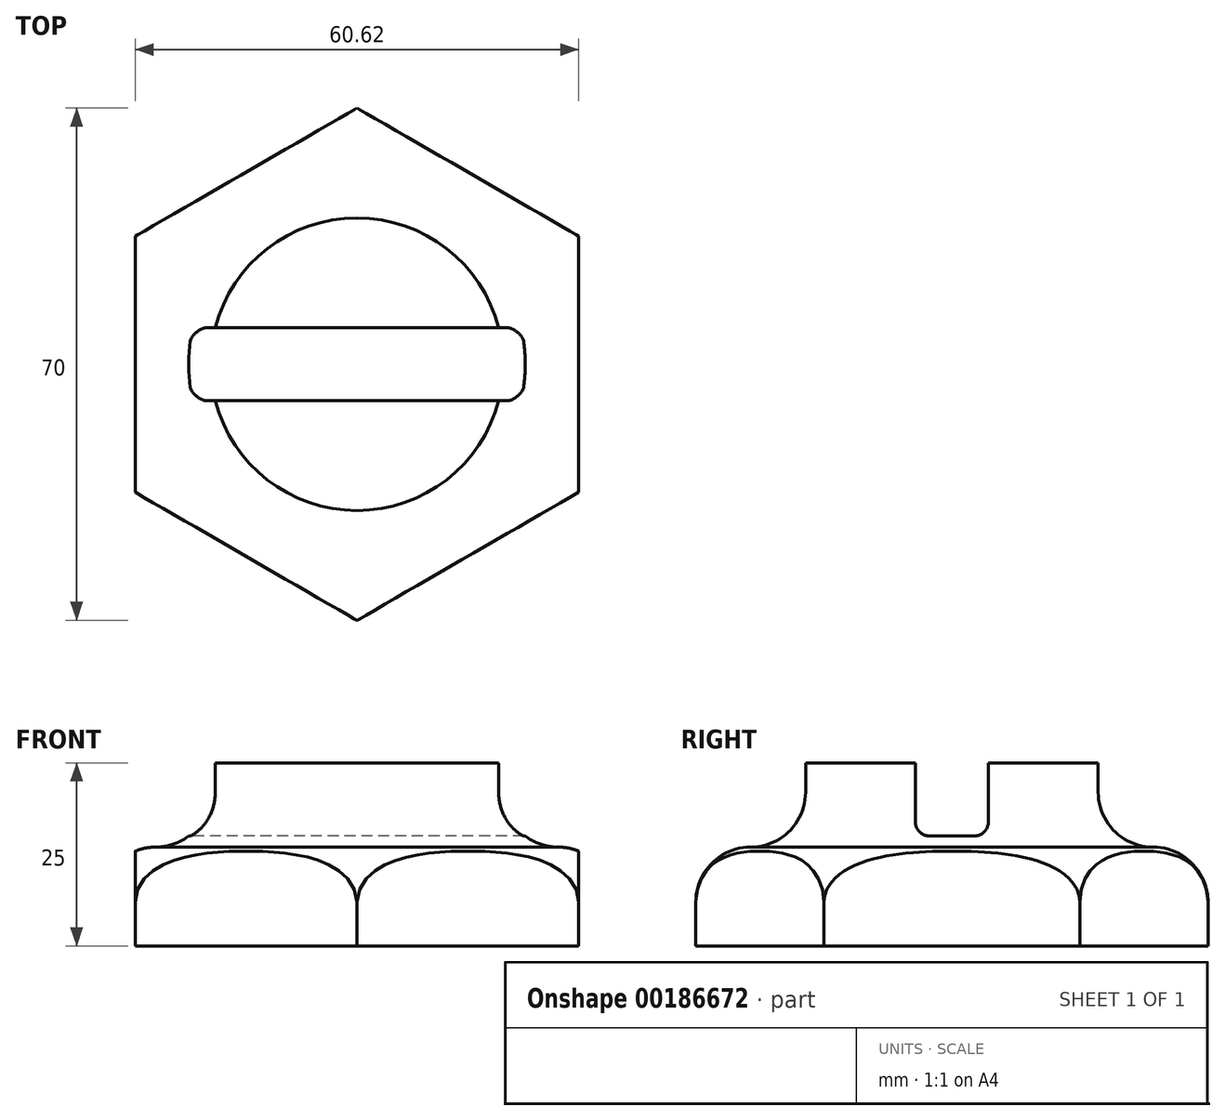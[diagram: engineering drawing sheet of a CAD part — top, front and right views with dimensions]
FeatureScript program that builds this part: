
annotation { "Feature Type Name" : "Feature", "Feature Type Description" : "" }
export const myFeature = defineFeature(function(context is Context, id is Id, definition is map)
    precondition{}
    {
        {
            var Q0;
            Q0=qCreatedBy(makeId("Top.planeOp"),FACE);
            var sketch = newSketch(context, id + "F0", { "sketchPlane" : qUnion([Q0])});
            skCircle(sketch, "E0.cCircle", {"center": v(0, 0) * mm, "radius": 35 * mm, "construction": true});
            skLineSegment(sketch, "E0.0", {"start": v(0, -35) * mm, "end": v(-30.31, -17.5) * mm});
            skLineSegment(sketch, "E0.1", {"start": v(-30.31, -17.5) * mm, "end": v(-30.31, 17.5) * mm});
            skLineSegment(sketch, "E0.2", {"start": v(-30.31, 17.5) * mm, "end": v(0, 35) * mm});
            skLineSegment(sketch, "E0.3", {"start": v(0, 35) * mm, "end": v(30.31, 17.5) * mm});
            skLineSegment(sketch, "E0.4", {"start": v(30.31, 17.5) * mm, "end": v(30.31, -17.5) * mm});
            skLineSegment(sketch, "E0.5", {"start": v(30.31, -17.5) * mm, "end": v(0, -35) * mm});
            skSolve(sketch);
        }
        {
            var Q0;
            Q0=qSketchRegion(id+"F0",true);
            extrude(context, id + "F1", {"entities" : qUnion([Q0]), "depth" : 25 * mm});
        }
        {
            var Q0;
            Q0=qCreatedBy(makeId("Right.planeOp"),FACE);
            var sketch = newSketch(context, id + "F2", { "sketchPlane" : qUnion([Q0])});
            skPoint(sketch, "E1.0", {"position": v(-35, 0) * mm});
            skLineSegment(sketch, "E2", {"start": v(-20, 21) * mm, "end": v(-20, 25) * mm});
            skArc(sketch, "E3", {"start": v(-27.5, 13.5) * mm, "mid": v(-32.8, 11.3) * mm, "end": v(-35, 6) * mm});
            skArc(sketch, "E4", {"start": v(-27.5, 13.5) * mm, "mid": v(-22.2, 15.7) * mm, "end": v(-20, 21) * mm});
            skLineSegment(sketch, "E5", {"start": v(-20, 25) * mm, "end": v(-17.5, 25) * mm});
            skLineSegment(sketch, "E6", {"start": v(-35, 6) * mm, "end": v(-35, 0) * mm});
            skLineSegment(sketch, "E7", {"start": v(-20, 25) * mm, "end": v(0, 25) * mm});
            skLineSegment(sketch, "E8", {"start": v(-35, 0) * mm, "end": v(0, 0) * mm});
            skLineSegment(sketch, "E9", {"start": v(0, 0) * mm, "end": v(0, 25) * mm});
            skSolve(sketch);
        }
        {
            var Q0;
            Q0=qCreatedBy(makeId("Right.planeOp"),FACE);
            var sketch = newSketch(context, id + "F3", { "sketchPlane" : qUnion([Q0])});
            skLineSegment(sketch, "E10", {"start": v(0, 0) * mm, "end": v(0, 25) * mm});
            skSolve(sketch);
        }
        {
            var Q0;
            Q0=qSketchRegion(id+"F2",true);
            var Q1;
            Q1=sQuery(id+"F3.wireOp",EDGE,"E10");
            revolve(context, id + "F4", {"operationType" : NewBodyOperationType.INTERSECT, "entities" : qUnion([Q0]), "axis" : qUnion([Q1]), "revolveType" : RevolveType.ONE_DIRECTION, "oppositeDirection" : true, "angle" : 360 * degree});
        }
        {
            var Q0;
            Q0=qCreatedBy(makeId("Right.planeOp"),FACE);
            var sketch = newSketch(context, id + "F5", { "sketchPlane" : qUnion([Q0])});
            skLineSegment(sketch, "E11", {"start": v(0, 0) * mm, "end": v(0, 25) * mm});
            skLineSegment(sketch, "E12", {"start": v(0, 25) * mm, "end": v(5, 25) * mm});
            skLineSegment(sketch, "E13", {"start": v(5, 25) * mm, "end": v(-5, 25) * mm});
            skLineSegment(sketch, "E14", {"start": v(-5, 25) * mm, "end": v(-5, 15) * mm});
            skLineSegment(sketch, "E15", {"start": v(-5, 15) * mm, "end": v(5, 15) * mm});
            skLineSegment(sketch, "E16", {"start": v(5, 15) * mm, "end": v(5, 25) * mm});
            skLineSegment(sketch, "E17.bottom", {"start": v(-5, 25) * mm, "end": v(5, 25) * mm});
            skLineSegment(sketch, "E17.right", {"start": v(5, 25) * mm, "end": v(5, 15) * mm});
            skSolve(sketch);
        }
        {
            var Q0;
            Q0=qSketchRegion(id+"F5",true);
            var Q1;
            Q1=makeQuery(id+"F1.opExtrude","SWEPT_FACE",FACE,{"disambiguationData":[OSD([sQuery(id+"F0.wireOp",EDGE,"E0.4")])]});
            extrude(context, id + "F6", {"entities" : qUnion([Q0, Q1]), "operationType" : NewBodyOperationType.REMOVE, "depth" : 49.5 * mm, "hasSecondDirection" : true, "secondDirectionOppositeDirection" : true, "secondDirectionDepth" : 25 * mm});
        }
        {
            var Q0;
            Q0=makeQuery(id+"F6.boolean.opBoolean","COPY",EDGE,{"derivedFrom":makeQuery(id+"F6.opExtrude","SWEPT_EDGE",EDGE,{"disambiguationData":[OSD([sQuery(id+"F5.wireOp",EDGE,"E15"),sQuery(id+"F5.wireOp",EDGE,"E17.right")])]})});
            var Q1;
            Q1=makeQuery(id+"F6.boolean.opBoolean","COPY",EDGE,{"derivedFrom":makeQuery(id+"F6.opExtrude","SWEPT_EDGE",EDGE,{"disambiguationData":[OSD([sQuery(id+"F5.wireOp",EDGE,"E15"),sQuery(id+"F5.wireOp",EDGE,"E14")])]})});
            fillet(context, id + "F7", {"entities" : qUnion([Q0, Q1]), "radius" : 2 * mm, "tangentPropagation" : true, "allowEdgeOverflow" : false});
        }
        {
            var Q0;
            Q0=makeQuery(id+"F6.boolean.opBoolean","COPY",FACE,{"derivedFrom":makeQuery(id+"F6.opExtrude","CAP_FACE",FACE,{"disambiguationData":[OSD([sQuery(id+"F0.wireOp",EDGE,"E0.4")])],"isStart":true})});
            extrude(context, id + "F8", {"entities" : qUnion([Q0]), "operationType" : NewBodyOperationType.ADD, "depth" : 25 * mm});
        }
    });
